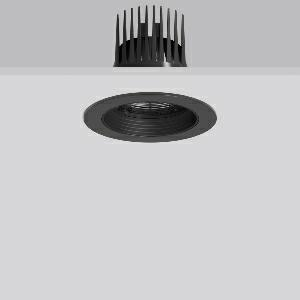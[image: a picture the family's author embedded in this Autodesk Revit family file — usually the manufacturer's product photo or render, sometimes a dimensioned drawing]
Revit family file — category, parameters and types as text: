
# Revit family: heledon_maxi_e_901769_003_3_76_1992
name_source: partatom
category: Lighting Fixtures
units: mm (PartAtom-declared; Revit-internal decimal feet)

## family parameters
Cut with Voids When Loaded = No
Host = Face
Light Source = No
Part Type = Normal
Room Calculation Point = No
Round Connector Dimension = Use Diameter
Shared = No

## types (1)
- HELEDON maxi E (1 x LED Modul 935, 3650 lm, 3500)
    Apparent Load = 35 VA
    Approval mark = CE
    CIE Flux Codes = 96 100 100 100 100
    Color Rendering = 92
    Color Temperature = 3500
    Default Elevation = 1800 mm
    Description = Series: HELEDON maxi
Round recessed downlight. Housing: die-cast aluminium, powder-coated. Black plastic ring and recessed LED to prevent glare from the side. Optical assembly with lens made of plastic (polycarbonate) for the best homogeneous light distribution - can be changed without tools. Best colour rendering index Ra>90. Suitable for Recessed ceiling mounting. Installation without tools thanks to spring fastening system. Including separate LED converter with connecting cable 600 mm.High quality converter without flickering and stroboscopic effect. Through-wiring box (5 pole) available as accessory. The following accessories can be mounted without use of tools: interchangeable lenses, decorative glasses, honeycomb louvre, clear and frosted diffusers, white interchangeable plastic ring. 
Colour: deep black, matt (RAL 9005)
Diameter: 162 mm
Height: 3 mm
Cut-out diameter: 152 mm
Recess height: 200 mm
Luminaire: recess height: 135 mm
Lamp: LED
Socket: without socket
Colour temperature: 3500K
Colour rendering index (CRI): 92
System power: 35 W
Rated luminous flux: 3650 lm
Luminous efficiency: 104 lm/W
Control gear: Converter, dimmable, DALI
Protection class: II
Type of protection: IP 20
    Height = 0 mm  [stored 0 ft]
    Lamp = 1 x LED Modul 935
    Lamp Light Flux = 3650 lm
    Lamp count = 1
    Length = 162 mm
    Lifetime = 50000 h
    Luminous efficacy = 104 lm/W
    Manufacturer = RZB
    ModVariant = No
    Model = 901769.003.3.76
    Mounting Place = Ceiling
    Mounting Type = Recessed
    Number of Poles = 1
    OnlyDefault = Yes
    Power Factor = 1
    Product Name = HELEDON maxi E
    Product group = Recessed downlights
    ProductGroupID = 402
    Protection Class = Protection class II
    Protection Degree = IP 20
    RLX_Detail_Level = 1
    RLX_Emergency_Light_Flux = 0 lm
    RLX_Emergency_Type = 0
    RLX_Emergency_Type_DB = No
    RlxData = <blob elided: 120921 chars, md5=ceb58632>
    Socket = socket
    Standby Power = 0 W
    System Light Flux = 3650 lm
    System Power = 35 W
    Type Comments = Product without accessories
    Type Image = 901663.003.jpg
    URL = http://relux.com
    VarID = ---
    Voltage = 230 V
    Voltage Range = 220-240 V
    Weight = 0.00 kg
    Width = 0 mm  [stored 0 ft]

note: [stored X ft] marks values corroborated as IEEE doubles in the binary element streams (Revit-internal decimal feet)

## geometry (parser evidence)
native form markers: Blend x4, Sweep x11
no freeform markers — native parametric forms only
